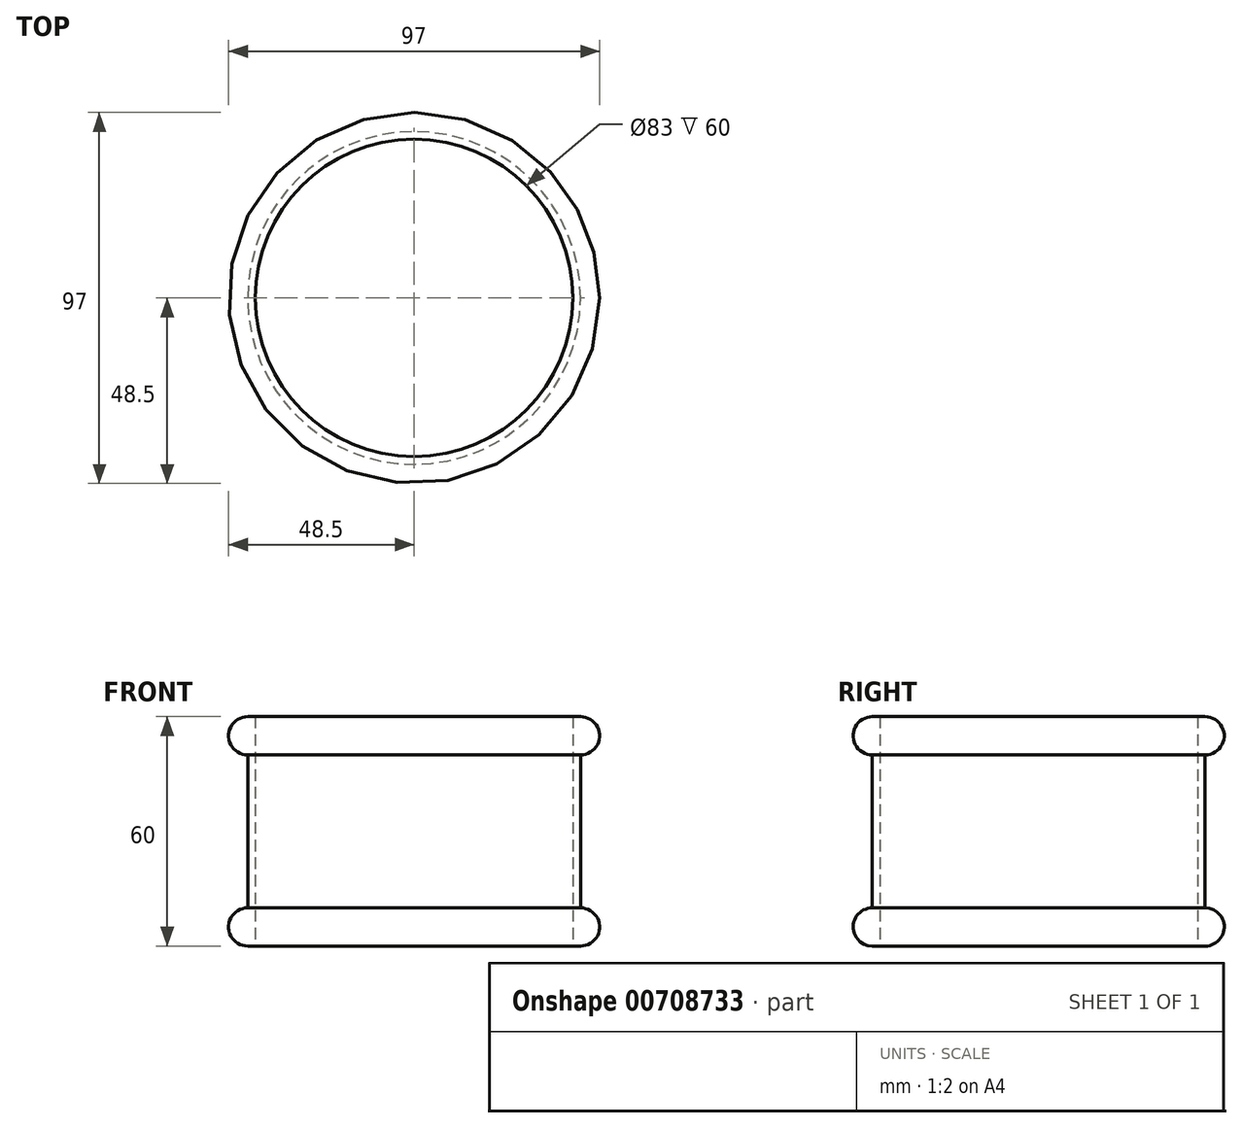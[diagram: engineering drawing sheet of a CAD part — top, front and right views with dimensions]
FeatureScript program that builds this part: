
annotation { "Feature Type Name" : "Feature", "Feature Type Description" : "" }
export const myFeature = defineFeature(function(context is Context, id is Id, definition is map)
    precondition{}
    {
        {
            var Q0;
            Q0=qCreatedBy(makeId("Top.planeOp"),FACE);
            var sketch = newSketch(context, id + "F0", { "sketchPlane" : qUnion([Q0])});
            skCircle(sketch, "E0", {"center": v(0, 0) * mm, "radius": 41.5 * mm});
            skCircle(sketch, "E1.0", {"center": v(0, 0) * mm, "radius": 43.5 * mm});
            skSolve(sketch);
        }
        {
            var Q0;
            Q0=makeQuery(id+"F0.imprint","IMPRINT",FACE,{"disambiguationData":[TD([[makeQuery(id+"F0.imprint","IMPRINT",EDGE,{"derivedFrom":sQuery(id+"F0.wireOp",EDGE,"E0")}),-1.0]])]});
            extrude(context, id + "F1", {"entities" : qUnion([Q0]), "depth" : 60 * mm, "offsetDistance" : 25 * mm});
        }
        {
            var Q0;
            Q0=qCreatedBy(makeId("Right.planeOp"),FACE);
            var sketch = newSketch(context, id + "F2", { "sketchPlane" : qUnion([Q0])});
            skArc(sketch, "E2", {"start": v(-43.5, 10) * mm, "mid": v(-48.5, 5) * mm, "end": v(-43.5, 0) * mm});
            skLineSegment(sketch, "E3", {"start": v(-43.5, 0) * mm, "end": v(-43.5, 10) * mm});
            skLineSegment(sketch, "E4", {"start": v(-71.95, 30) * mm, "end": v(34.52, 30) * mm});
            skArc(sketch, "E5.MirrorCS", {"start": v(-43.5, 50) * mm, "mid": v(-48.5, 55) * mm, "end": v(-43.5, 60) * mm});
            skLineSegment(sketch, "E6.MirrorCS", {"start": v(-43.5, 60) * mm, "end": v(-43.5, 50) * mm});
            skLineSegment(sketch, "E7", {"start": v(0, 74.16) * mm, "end": v(0, 0) * mm});
            skSolve(sketch);
        }
        {
            var Q0;
            Q0 = qSketchRegion(id + "F2", true);
            var Q1;
            Q1=sQuery(id+"F2.wireOp",EDGE,"E7");
            revolve(context, id + "F3", {"operationType" : NewBodyOperationType.ADD, "surfaceOperationType" : NewSurfaceOperationType.NEW, "entities" : qUnion([Q0]), "axis" : qUnion([Q1]), "revolveType" : RevolveType.FULL});
        }
    });
